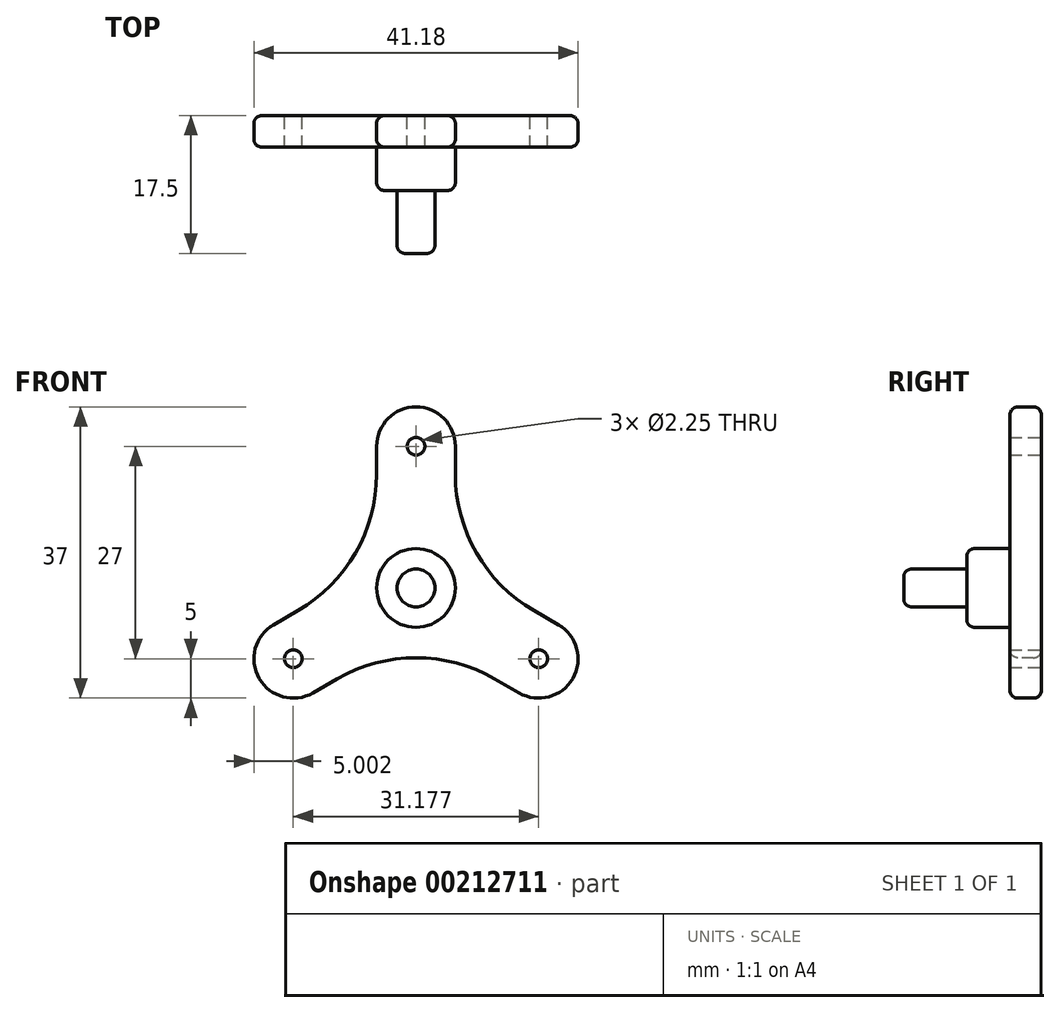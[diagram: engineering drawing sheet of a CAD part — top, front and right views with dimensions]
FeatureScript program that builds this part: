
annotation { "Feature Type Name" : "Feature", "Feature Type Description" : "" }
export const myFeature = defineFeature(function(context is Context, id is Id, definition is map)
    precondition{}
    {
        {
            var Q0;
            Q0=qCreatedBy(makeId("Front.planeOp"),FACE);
            var sketch = newSketch(context, id + "F0", { "sketchPlane" : qUnion([Q0])});
            skCircle(sketch, "E0", {"center": v(0, 0) * mm, "radius": 18 * mm, "construction": true});
            skArc(sketch, "E1", {"start": v(4.95, 17.3) * mm, "mid": v(0, 23) * mm, "end": v(-4.95, 17.3) * mm});
            skLineSegment(sketch, "E2", {"start": v(-5, 18) * mm, "end": v(-5, 0) * mm});
            skLineSegment(sketch, "E3", {"start": v(-5, 0) * mm, "end": v(5, 0) * mm});
            skLineSegment(sketch, "E4", {"start": v(5, 0) * mm, "end": v(5, 18) * mm});
            skArc(sketch, "E5.1.0", {"start": v(-17.46, -4.36) * mm, "mid": v(-19.92, -11.5) * mm, "end": v(-12.51, -12.94) * mm});
            skLineSegment(sketch, "E5.1.1", {"start": v(-13.09, -13.33) * mm, "end": v(2.5, -4.33) * mm});
            skLineSegment(sketch, "E5.1.2", {"start": v(-2.5, 4.33) * mm, "end": v(-18.09, -4.67) * mm});
            skLineSegment(sketch, "E5.1.3", {"start": v(2.5, -4.33) * mm, "end": v(-2.5, 4.33) * mm});
            skArc(sketch, "E5.2.0", {"start": v(12.51, -12.94) * mm, "mid": v(19.92, -11.5) * mm, "end": v(17.46, -4.36) * mm});
            skLineSegment(sketch, "E5.2.1", {"start": v(18.09, -4.67) * mm, "end": v(2.5, 4.33) * mm});
            skLineSegment(sketch, "E5.2.2", {"start": v(-2.5, -4.33) * mm, "end": v(13.09, -13.33) * mm});
            skLineSegment(sketch, "E5.2.3", {"start": v(2.5, 4.33) * mm, "end": v(-2.5, -4.33) * mm});
            skCircle(sketch, "E6", {"center": v(0, 18) * mm, "radius": 1.13 * mm});
            skCircle(sketch, "E7.1.0", {"center": v(-15.59, -9) * mm, "radius": 1.13 * mm});
            skCircle(sketch, "E7.2.0", {"center": v(15.59, -9) * mm, "radius": 1.13 * mm});
            skSolve(sketch);
        }
        {
            var Q0;
            Q0 = qSketchRegion(id + "F0", true);
            extrude(context, id + "F1", {"entities" : qUnion([Q0]), "depth" : 4 * mm, "offsetDistance" : 25 * mm});
        }
        {
            var Q0;
            Q0=makeQuery(id+"F1.opExtrude","SWEPT_EDGE",EDGE,{"disambiguationData":[OSD([sQuery(id+"F0.wireOp",EDGE,"E2"),sQuery(id+"F0.wireOp",EDGE,"E5.1.2")])]});
            var Q1;
            Q1=makeQuery(id+"F1.opExtrude","SWEPT_EDGE",EDGE,{"disambiguationData":[OSD([sQuery(id+"F0.wireOp",EDGE,"E4"),sQuery(id+"F0.wireOp",EDGE,"E5.2.1")])]});
            var Q2;
            Q2=makeQuery(id+"F1.opExtrude","SWEPT_EDGE",EDGE,{"disambiguationData":[OSD([sQuery(id+"F0.wireOp",EDGE,"E5.1.1"),sQuery(id+"F0.wireOp",EDGE,"E5.2.2")])]});
            fillet(context, id + "F2", {"entities" : qUnion([Q0, Q1, Q2]), "tangentPropagation" : true, "radius" : 20 * mm, "defaultsChanged" : true, "vertexSettings" : [], "allowEdgeOverflow" : false});
        }
        {
            var Q0;
            Q0=makeQuery(id+"F1.opExtrude","CAP_FACE",FACE,{"disambiguationData":[OSD([sQuery(id+"F0.wireOp",EDGE,"E1"),sQuery(id+"F0.wireOp",EDGE,"E2"),sQuery(id+"F0.wireOp",EDGE,"E4"),sQuery(id+"F0.wireOp",EDGE,"E5.1.0"),sQuery(id+"F0.wireOp",EDGE,"E5.1.1"),sQuery(id+"F0.wireOp",EDGE,"E5.1.2"),sQuery(id+"F0.wireOp",EDGE,"E5.2.0"),sQuery(id+"F0.wireOp",EDGE,"E5.2.1"),sQuery(id+"F0.wireOp",EDGE,"E5.2.2"),sQuery(id+"F0.wireOp",EDGE,"E6"),sQuery(id+"F0.wireOp",EDGE,"E7.1.0"),sQuery(id+"F0.wireOp",EDGE,"E7.2.0")])],"isStart":false});
            var sketch = newSketch(context, id + "F3", { "sketchPlane" : qUnion([Q0])});
            skCircle(sketch, "E8", {"center": v(0, 0) * mm, "radius": 5 * mm});
            skSolve(sketch);
        }
        {
            var Q0;
            Q0 = qSketchRegion(id + "F3", true);
            extrude(context, id + "F4", {"entities" : qUnion([Q0]), "operationType" : NewBodyOperationType.ADD, "depth" : 5.5 * mm, "offsetDistance" : 25 * mm});
        }
        {
            var Q0;
            {var subQ0=sQuery(id+"F0.wireOp",EDGE,"E5.1.2");var subQ1=sQuery(id+"F0.wireOp",EDGE,"E2");Q0=makeQuery(id+"F2.opFillet","BLEND_EDGE",EDGE,{"blendedFrom":[makeQuery(id+"F1.opExtrude","SWEPT_EDGE",EDGE,{"disambiguationData":[OSD([subQ1,subQ0])]}),makeQuery(id+"F1.opExtrude","CAP_FACE",FACE,{"disambiguationData":[OSD([sQuery(id+"F0.wireOp",EDGE,"E1"),subQ1,sQuery(id+"F0.wireOp",EDGE,"E4"),sQuery(id+"F0.wireOp",EDGE,"E5.1.0"),sQuery(id+"F0.wireOp",EDGE,"E5.1.1"),subQ0,sQuery(id+"F0.wireOp",EDGE,"E5.2.0"),sQuery(id+"F0.wireOp",EDGE,"E5.2.1"),sQuery(id+"F0.wireOp",EDGE,"E5.2.2"),sQuery(id+"F0.wireOp",EDGE,"E6"),sQuery(id+"F0.wireOp",EDGE,"E7.1.0"),sQuery(id+"F0.wireOp",EDGE,"E7.2.0")])],"isStart":true})],"blendedInto":[makeQuery(id+"F1.opExtrude","CAP_FACE",FACE,{"disambiguationData":[OSD([sQuery(id+"F0.wireOp",EDGE,"E1"),subQ1,sQuery(id+"F0.wireOp",EDGE,"E4"),sQuery(id+"F0.wireOp",EDGE,"E5.1.0"),sQuery(id+"F0.wireOp",EDGE,"E5.1.1"),subQ0,sQuery(id+"F0.wireOp",EDGE,"E5.2.0"),sQuery(id+"F0.wireOp",EDGE,"E5.2.1"),sQuery(id+"F0.wireOp",EDGE,"E5.2.2"),sQuery(id+"F0.wireOp",EDGE,"E6"),sQuery(id+"F0.wireOp",EDGE,"E7.1.0"),sQuery(id+"F0.wireOp",EDGE,"E7.2.0")])],"isStart":true})]});}
            var Q1;
            {var subQ0=sQuery(id+"F0.wireOp",EDGE,"E5.1.2");var subQ1=sQuery(id+"F0.wireOp",EDGE,"E2");Q1=makeQuery(id+"F2.opFillet","BLEND_EDGE",EDGE,{"blendedFrom":[makeQuery(id+"F1.opExtrude","SWEPT_EDGE",EDGE,{"disambiguationData":[OSD([subQ1,subQ0])]}),makeQuery(id+"F1.opExtrude","CAP_FACE",FACE,{"disambiguationData":[OSD([sQuery(id+"F0.wireOp",EDGE,"E1"),subQ1,sQuery(id+"F0.wireOp",EDGE,"E4"),sQuery(id+"F0.wireOp",EDGE,"E5.1.0"),sQuery(id+"F0.wireOp",EDGE,"E5.1.1"),subQ0,sQuery(id+"F0.wireOp",EDGE,"E5.2.0"),sQuery(id+"F0.wireOp",EDGE,"E5.2.1"),sQuery(id+"F0.wireOp",EDGE,"E5.2.2"),sQuery(id+"F0.wireOp",EDGE,"E6"),sQuery(id+"F0.wireOp",EDGE,"E7.1.0"),sQuery(id+"F0.wireOp",EDGE,"E7.2.0")])],"isStart":false})],"blendedInto":[makeQuery(id+"F1.opExtrude","CAP_FACE",FACE,{"disambiguationData":[OSD([sQuery(id+"F0.wireOp",EDGE,"E1"),subQ1,sQuery(id+"F0.wireOp",EDGE,"E4"),sQuery(id+"F0.wireOp",EDGE,"E5.1.0"),sQuery(id+"F0.wireOp",EDGE,"E5.1.1"),subQ0,sQuery(id+"F0.wireOp",EDGE,"E5.2.0"),sQuery(id+"F0.wireOp",EDGE,"E5.2.1"),sQuery(id+"F0.wireOp",EDGE,"E5.2.2"),sQuery(id+"F0.wireOp",EDGE,"E6"),sQuery(id+"F0.wireOp",EDGE,"E7.1.0"),sQuery(id+"F0.wireOp",EDGE,"E7.2.0")])],"isStart":false})]});}
            fillet(context, id + "F5", {"entities" : qUnion([Q0, Q1]), "tangentPropagation" : true, "radius" : 1 * mm, "defaultsChanged" : false, "vertexSettings" : [], "allowEdgeOverflow" : false});
        }
        {
            var Q0;
            Q0=makeQuery(id+"F4.opExtrude","CAP_FACE",FACE,{"disambiguationData":[OSD([sQuery(id+"F3.wireOp",EDGE,"E8")])],"isStart":false});
            var sketch = newSketch(context, id + "F6", { "sketchPlane" : qUnion([Q0])});
            skCircle(sketch, "E9", {"center": v(0, 0) * mm, "radius": 2.4 * mm});
            skSolve(sketch);
        }
        {
            var Q0;
            Q0=makeQuery(id+"F6.imprint","IMPRINT",FACE,{"disambiguationData":[TD([[makeQuery(id+"F6.imprint","IMPRINT",EDGE,{"derivedFrom":sQuery(id+"F6.wireOp",EDGE,"E9")}),1.0]])]});
            extrude(context, id + "F7", {"entities" : qUnion([Q0]), "operationType" : NewBodyOperationType.ADD, "depth" : 8 * mm, "offsetDistance" : 25 * mm});
        }
        {
            var Q0;
            Q0=makeQuery(id+"F4.opExtrude","CAP_EDGE",EDGE,{"disambiguationData":[OSD([sQuery(id+"F3.wireOp",EDGE,"E8")])],"isStart":true});
            var Q1;
            Q1=makeQuery(id+"F4.opExtrude","CAP_EDGE",EDGE,{"disambiguationData":[OSD([sQuery(id+"F3.wireOp",EDGE,"E8")])],"isStart":false});
            var Q2;
            Q2=makeQuery(id+"F7.opExtrude","CAP_EDGE",EDGE,{"disambiguationData":[OSD([sQuery(id+"F6.wireOp",EDGE,"E9")])],"isStart":false});
            fillet(context, id + "F8", {"entities" : qUnion([Q0, Q1, Q2]), "tangentPropagation" : true, "radius" : 1 * mm, "defaultsChanged" : false, "vertexSettings" : [], "allowEdgeOverflow" : false});
        }
    });
